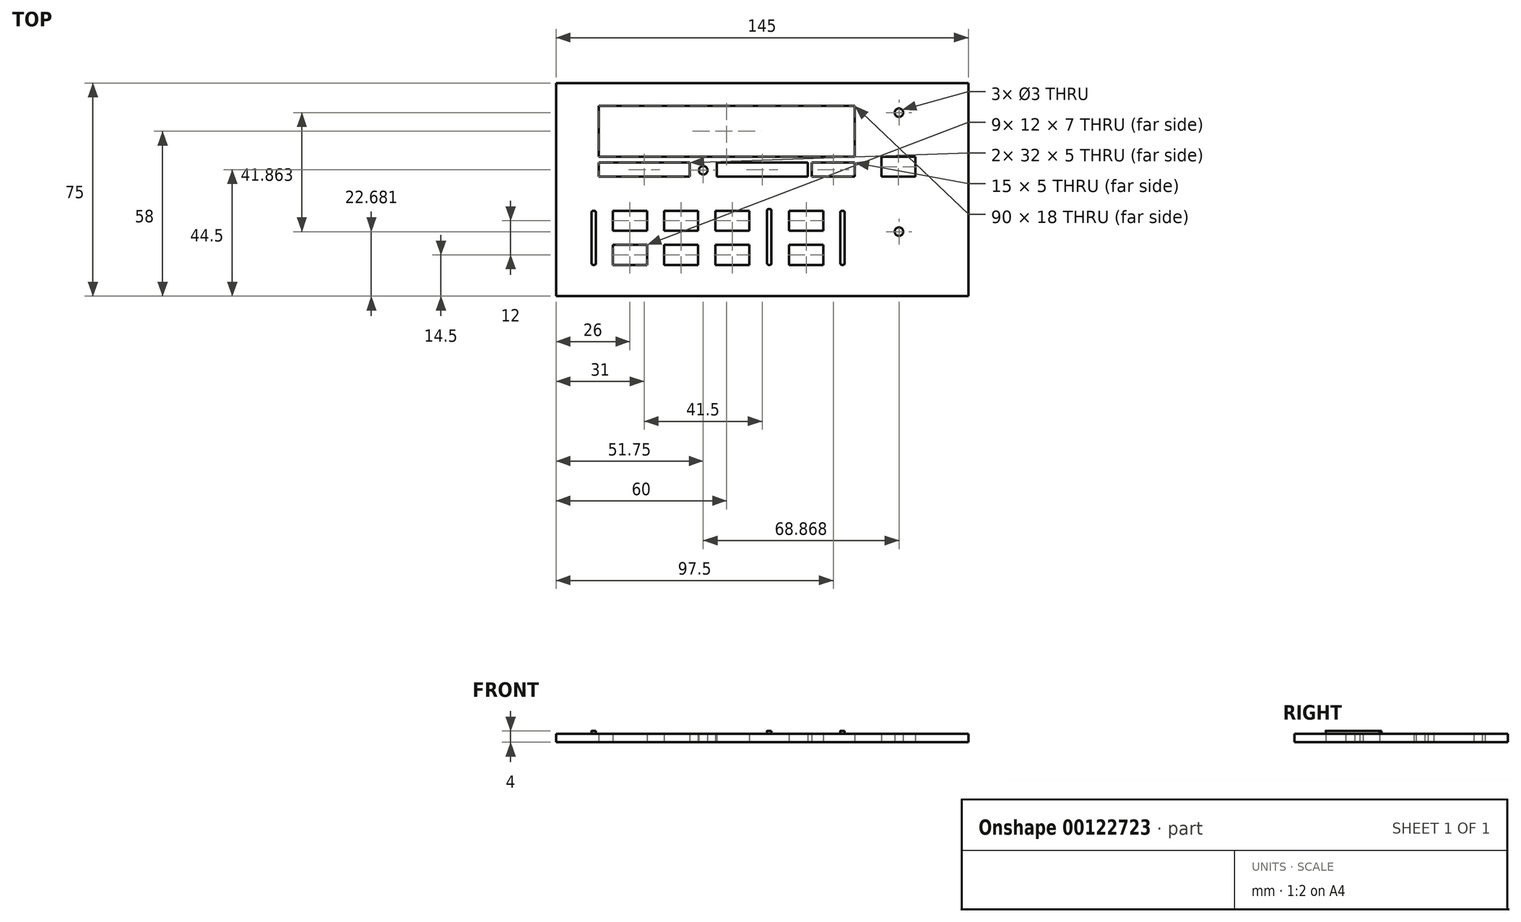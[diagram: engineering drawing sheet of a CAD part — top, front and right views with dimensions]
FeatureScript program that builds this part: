
annotation { "Feature Type Name" : "Feature", "Feature Type Description" : "" }
export const myFeature = defineFeature(function(context is Context, id is Id, definition is map)
    precondition{}
    {
        {
            var Q0;
            Q0=qCreatedBy(makeId("Top.planeOp"),FACE);
            var sketch = newSketch(context, id + "F0", { "sketchPlane" : qUnion([Q0])});
            skLineSegment(sketch, "E0.bottom", {"start": v(0, 0) * mm, "end": v(145, 0) * mm});
            skLineSegment(sketch, "E0.left", {"start": v(0, 0) * mm, "end": v(0, -75) * mm});
            skLineSegment(sketch, "E0.right", {"start": v(145, 0) * mm, "end": v(145, -75) * mm});
            skLineSegment(sketch, "E1.bottom", {"start": v(15, -8) * mm, "end": v(105, -8) * mm});
            skLineSegment(sketch, "E1.top", {"start": v(15, -26) * mm, "end": v(105, -26) * mm});
            skLineSegment(sketch, "E1.left", {"start": v(15, -8) * mm, "end": v(15, -26) * mm});
            skLineSegment(sketch, "E1.right", {"start": v(105, -8) * mm, "end": v(105, -26) * mm});
            skCircle(sketch, "E2", {"center": v(120.62, -10.46) * mm, "radius": 7 * mm, "construction": true});
            skCircle(sketch, "E3", {"center": v(120.62, -10.46) * mm, "radius": 1.5 * mm});
            skCircle(sketch, "E4", {"center": v(120.62, -52.32) * mm, "radius": 8.5 * mm, "construction": true});
            skCircle(sketch, "E5", {"center": v(120.62, -52.32) * mm, "radius": 1.5 * mm});
            skLineSegment(sketch, "E6.bottom", {"start": v(114.43, -26) * mm, "end": v(126.43, -26) * mm});
            skLineSegment(sketch, "E6.top", {"start": v(114.43, -33) * mm, "end": v(126.43, -33) * mm});
            skLineSegment(sketch, "E6.left", {"start": v(114.43, -26) * mm, "end": v(114.43, -33) * mm});
            skLineSegment(sketch, "E6.right", {"start": v(126.43, -26) * mm, "end": v(126.43, -33) * mm});
            skLineSegment(sketch, "E7.bottom", {"start": v(15, -28) * mm, "end": v(47, -28) * mm});
            skLineSegment(sketch, "E7.top", {"start": v(15, -33) * mm, "end": v(47, -33) * mm});
            skLineSegment(sketch, "E7.left", {"start": v(15, -28) * mm, "end": v(15, -33) * mm});
            skLineSegment(sketch, "E7.right", {"start": v(47, -28) * mm, "end": v(47, -33) * mm});
            skLineSegment(sketch, "E8.bottom", {"start": v(56.5, -28) * mm, "end": v(88.5, -28) * mm});
            skLineSegment(sketch, "E8.top", {"start": v(56.5, -33) * mm, "end": v(88.5, -33) * mm});
            skLineSegment(sketch, "E8.left", {"start": v(56.5, -28) * mm, "end": v(56.5, -33) * mm});
            skLineSegment(sketch, "E8.right", {"start": v(88.5, -28) * mm, "end": v(88.5, -33) * mm});
            skLineSegment(sketch, "E9.bottom", {"start": v(105, -28) * mm, "end": v(90, -28) * mm});
            skLineSegment(sketch, "E9.top", {"start": v(105, -33) * mm, "end": v(90, -33) * mm});
            skLineSegment(sketch, "E9.left", {"start": v(105, -28) * mm, "end": v(105, -33) * mm});
            skLineSegment(sketch, "E9.right", {"start": v(90, -28) * mm, "end": v(90, -33) * mm});
            skCircle(sketch, "E10", {"center": v(51.75, -30.72) * mm, "radius": 1.5 * mm});
            skLineSegment(sketch, "E11.bottom", {"start": v(38, -45) * mm, "end": v(50, -45) * mm});
            skLineSegment(sketch, "E11.top", {"start": v(38, -52) * mm, "end": v(50, -52) * mm});
            skLineSegment(sketch, "E11.left", {"start": v(38, -45) * mm, "end": v(38, -52) * mm});
            skLineSegment(sketch, "E11.right", {"start": v(50, -45) * mm, "end": v(50, -52) * mm});
            skLineSegment(sketch, "E12.bottom", {"start": v(56, -45) * mm, "end": v(68, -45) * mm});
            skLineSegment(sketch, "E12.top", {"start": v(56, -52) * mm, "end": v(68, -52) * mm});
            skLineSegment(sketch, "E12.left", {"start": v(56, -45) * mm, "end": v(56, -52) * mm});
            skLineSegment(sketch, "E12.right", {"start": v(68, -45) * mm, "end": v(68, -52) * mm});
            skLineSegment(sketch, "E13.bottom", {"start": v(20, -45) * mm, "end": v(32, -45) * mm});
            skLineSegment(sketch, "E13.top", {"start": v(20, -52) * mm, "end": v(32, -52) * mm});
            skLineSegment(sketch, "E13.left", {"start": v(20, -45) * mm, "end": v(20, -52) * mm});
            skLineSegment(sketch, "E13.right", {"start": v(32, -45) * mm, "end": v(32, -52) * mm});
            skLineSegment(sketch, "E14.bottom", {"start": v(20, -57) * mm, "end": v(32, -57) * mm});
            skLineSegment(sketch, "E14.top", {"start": v(20, -64) * mm, "end": v(32, -64) * mm});
            skLineSegment(sketch, "E14.left", {"start": v(20, -57) * mm, "end": v(20, -64) * mm});
            skLineSegment(sketch, "E14.right", {"start": v(32, -57) * mm, "end": v(32, -64) * mm});
            skLineSegment(sketch, "E15.bottom", {"start": v(38, -57) * mm, "end": v(50, -57) * mm});
            skLineSegment(sketch, "E15.top", {"start": v(38, -64) * mm, "end": v(50, -64) * mm});
            skLineSegment(sketch, "E15.left", {"start": v(38, -57) * mm, "end": v(38, -64) * mm});
            skLineSegment(sketch, "E15.right", {"start": v(50, -57) * mm, "end": v(50, -64) * mm});
            skLineSegment(sketch, "E16", {"start": v(0, -75) * mm, "end": v(145, -75) * mm});
            skLineSegment(sketch, "E17", {"start": v(56, -57) * mm, "end": v(56, -64) * mm});
            skLineSegment(sketch, "E18", {"start": v(56, -64) * mm, "end": v(68, -64) * mm});
            skLineSegment(sketch, "E19", {"start": v(68, -64) * mm, "end": v(68, -57) * mm});
            skLineSegment(sketch, "E20", {"start": v(68, -57) * mm, "end": v(56, -57) * mm});
            skLineSegment(sketch, "E21.bottom", {"start": v(82, -57) * mm, "end": v(94, -57) * mm});
            skLineSegment(sketch, "E21.top", {"start": v(82, -64) * mm, "end": v(94, -64) * mm});
            skLineSegment(sketch, "E21.left", {"start": v(82, -57) * mm, "end": v(82, -64) * mm});
            skLineSegment(sketch, "E21.right", {"start": v(94, -57) * mm, "end": v(94, -64) * mm});
            skLineSegment(sketch, "E22.bottom", {"start": v(82, -45) * mm, "end": v(94, -45) * mm});
            skLineSegment(sketch, "E22.top", {"start": v(82, -52) * mm, "end": v(94, -52) * mm});
            skLineSegment(sketch, "E22.left", {"start": v(82, -45) * mm, "end": v(82, -52) * mm});
            skLineSegment(sketch, "E22.right", {"start": v(94, -45) * mm, "end": v(94, -52) * mm});
            skSolve(sketch);
        }
        {
            var Q0;
            Q0=makeQuery(id+"F0.imprint","IMPRINT",FACE,{"disambiguationData":[TD([[makeQuery(id+"F0.imprint","IMPRINT",EDGE,{"derivedFrom":sQuery(id+"F0.wireOp",EDGE,"E0.bottom")}),-1.0]])]});
            extrude(context, id + "F1", {"entities" : qUnion([Q0]), "depth" : 3 * mm});
        }
        {
            var Q0;
            Q0=makeQuery(id+"F1.opExtrude","CAP_FACE",FACE,{"disambiguationData":[OSD([sQuery(id+"F0.wireOp",EDGE,"E0.bottom"),sQuery(id+"F0.wireOp",EDGE,"E0.left"),sQuery(id+"F0.wireOp",EDGE,"E0.right"),sQuery(id+"F0.wireOp",EDGE,"E1.bottom"),sQuery(id+"F0.wireOp",EDGE,"E1.top"),sQuery(id+"F0.wireOp",EDGE,"E1.left"),sQuery(id+"F0.wireOp",EDGE,"E1.right"),sQuery(id+"F0.wireOp",EDGE,"E3"),sQuery(id+"F0.wireOp",EDGE,"E5"),sQuery(id+"F0.wireOp",EDGE,"E6.bottom"),sQuery(id+"F0.wireOp",EDGE,"E6.top"),sQuery(id+"F0.wireOp",EDGE,"E6.left"),sQuery(id+"F0.wireOp",EDGE,"E6.right"),sQuery(id+"F0.wireOp",EDGE,"E7.bottom"),sQuery(id+"F0.wireOp",EDGE,"E7.top"),sQuery(id+"F0.wireOp",EDGE,"E7.left"),sQuery(id+"F0.wireOp",EDGE,"E7.right"),sQuery(id+"F0.wireOp",EDGE,"E8.bottom"),sQuery(id+"F0.wireOp",EDGE,"E8.top"),sQuery(id+"F0.wireOp",EDGE,"E8.left"),sQuery(id+"F0.wireOp",EDGE,"E8.right"),sQuery(id+"F0.wireOp",EDGE,"E9.bottom"),sQuery(id+"F0.wireOp",EDGE,"E9.top"),sQuery(id+"F0.wireOp",EDGE,"E9.left"),sQuery(id+"F0.wireOp",EDGE,"E9.right"),sQuery(id+"F0.wireOp",EDGE,"E10"),sQuery(id+"F0.wireOp",EDGE,"E11.bottom"),sQuery(id+"F0.wireOp",EDGE,"E11.top"),sQuery(id+"F0.wireOp",EDGE,"E11.left"),sQuery(id+"F0.wireOp",EDGE,"E11.right"),sQuery(id+"F0.wireOp",EDGE,"E12.bottom"),sQuery(id+"F0.wireOp",EDGE,"E12.top"),sQuery(id+"F0.wireOp",EDGE,"E12.left"),sQuery(id+"F0.wireOp",EDGE,"E12.right"),sQuery(id+"F0.wireOp",EDGE,"E13.bottom"),sQuery(id+"F0.wireOp",EDGE,"E13.top"),sQuery(id+"F0.wireOp",EDGE,"E13.left"),sQuery(id+"F0.wireOp",EDGE,"E13.right"),sQuery(id+"F0.wireOp",EDGE,"E14.bottom"),sQuery(id+"F0.wireOp",EDGE,"E14.top"),sQuery(id+"F0.wireOp",EDGE,"E14.left"),sQuery(id+"F0.wireOp",EDGE,"E14.right"),sQuery(id+"F0.wireOp",EDGE,"E15.bottom"),sQuery(id+"F0.wireOp",EDGE,"E15.top"),sQuery(id+"F0.wireOp",EDGE,"E15.left"),sQuery(id+"F0.wireOp",EDGE,"E15.right"),sQuery(id+"F0.wireOp",EDGE,"E16"),sQuery(id+"F0.wireOp",EDGE,"E17"),sQuery(id+"F0.wireOp",EDGE,"E18"),sQuery(id+"F0.wireOp",EDGE,"E19"),sQuery(id+"F0.wireOp",EDGE,"E20"),sQuery(id+"F0.wireOp",EDGE,"E21.bottom"),sQuery(id+"F0.wireOp",EDGE,"E21.top"),sQuery(id+"F0.wireOp",EDGE,"E21.left"),sQuery(id+"F0.wireOp",EDGE,"E21.right"),sQuery(id+"F0.wireOp",EDGE,"E22.bottom"),sQuery(id+"F0.wireOp",EDGE,"E22.top"),sQuery(id+"F0.wireOp",EDGE,"E22.left"),sQuery(id+"F0.wireOp",EDGE,"E22.right")])],"isStart":false});
            var sketch = newSketch(context, id + "F2", { "sketchPlane" : qUnion([Q0])});
            skLineSegment(sketch, "E23.bottom", {"start": v(13, -45) * mm, "end": v(13.5, -45) * mm});
            skLineSegment(sketch, "E23.top", {"start": v(13, -64) * mm, "end": v(13.5, -64) * mm});
            skLineSegment(sketch, "E23.left", {"start": v(12.5, -45.5) * mm, "end": v(12.5, -63.5) * mm});
            skLineSegment(sketch, "E23.right", {"start": v(14, -45.5) * mm, "end": v(14, -63.5) * mm});
            skLineSegment(sketch, "E24.bottom", {"start": v(100.5, -45) * mm, "end": v(101, -45) * mm});
            skLineSegment(sketch, "E24.top", {"start": v(100.5, -64) * mm, "end": v(101, -64) * mm});
            skLineSegment(sketch, "E24.left", {"start": v(101.5, -45.5) * mm, "end": v(101.5, -63.5) * mm});
            skLineSegment(sketch, "E24.right", {"start": v(100, -45.5) * mm, "end": v(100, -63.5) * mm});
            skLineSegment(sketch, "E25.bottom", {"start": v(74.75, -44.36) * mm, "end": v(75.25, -44.36) * mm});
            skLineSegment(sketch, "E25.top", {"start": v(74.75, -64) * mm, "end": v(75.25, -64) * mm});
            skLineSegment(sketch, "E25.left", {"start": v(74.25, -44.86) * mm, "end": v(74.25, -63.5) * mm});
            skLineSegment(sketch, "E25.right", {"start": v(75.75, -44.86) * mm, "end": v(75.75, -63.5) * mm});
            skPoint(sketch, "E26.visualSharp", {"position": v(12.5, -45) * mm});
            skArc(sketch, "E26.filletArc", {"start": v(13, -45) * mm, "mid": v(12.65, -45.15) * mm, "end": v(12.5, -45.5) * mm});
            skPoint(sketch, "E27.visualSharp", {"position": v(14, -45) * mm});
            skArc(sketch, "E27.filletArc", {"start": v(14, -45.5) * mm, "mid": v(13.85, -45.15) * mm, "end": v(13.5, -45) * mm});
            skPoint(sketch, "E28.visualSharp", {"position": v(12.5, -64) * mm});
            skArc(sketch, "E28.filletArc", {"start": v(12.5, -63.5) * mm, "mid": v(12.65, -63.85) * mm, "end": v(13, -64) * mm});
            skPoint(sketch, "E29.visualSharp", {"position": v(14, -64) * mm});
            skArc(sketch, "E29.filletArc", {"start": v(13.5, -64) * mm, "mid": v(13.85, -63.85) * mm, "end": v(14, -63.5) * mm});
            skPoint(sketch, "E30.visualSharp", {"position": v(74.25, -44.36) * mm});
            skArc(sketch, "E30.filletArc", {"start": v(74.75, -44.36) * mm, "mid": v(74.4, -44.51) * mm, "end": v(74.25, -44.86) * mm});
            skPoint(sketch, "E31.visualSharp", {"position": v(75.75, -44.36) * mm});
            skArc(sketch, "E31.filletArc", {"start": v(75.75, -44.86) * mm, "mid": v(75.6, -44.51) * mm, "end": v(75.25, -44.36) * mm});
            skPoint(sketch, "E32.visualSharp", {"position": v(74.25, -64) * mm});
            skArc(sketch, "E32.filletArc", {"start": v(74.25, -63.5) * mm, "mid": v(74.4, -63.85) * mm, "end": v(74.75, -64) * mm});
            skPoint(sketch, "E33.visualSharp", {"position": v(75.75, -64) * mm});
            skArc(sketch, "E33.filletArc", {"start": v(75.25, -64) * mm, "mid": v(75.6, -63.85) * mm, "end": v(75.75, -63.5) * mm});
            skPoint(sketch, "E34.visualSharp", {"position": v(100, -45) * mm});
            skArc(sketch, "E34.filletArc", {"start": v(100.5, -45) * mm, "mid": v(100.15, -45.15) * mm, "end": v(100, -45.5) * mm});
            skPoint(sketch, "E35.visualSharp", {"position": v(101.5, -45) * mm});
            skArc(sketch, "E35.filletArc", {"start": v(101.5, -45.5) * mm, "mid": v(101.35, -45.15) * mm, "end": v(101, -45) * mm});
            skPoint(sketch, "E36.visualSharp", {"position": v(100, -64) * mm});
            skArc(sketch, "E36.filletArc", {"start": v(100, -63.5) * mm, "mid": v(100.15, -63.85) * mm, "end": v(100.5, -64) * mm});
            skPoint(sketch, "E37.visualSharp", {"position": v(101.5, -64) * mm});
            skArc(sketch, "E37.filletArc", {"start": v(101, -64) * mm, "mid": v(101.35, -63.85) * mm, "end": v(101.5, -63.5) * mm});
            skSolve(sketch);
        }
        {
            var Q0;
            Q0=qSketchRegion(id+"F2",true);
            extrude(context, id + "F3", {"entities" : qUnion([Q0]), "operationType" : NewBodyOperationType.ADD, "depth" : 1 * mm});
        }
    });
